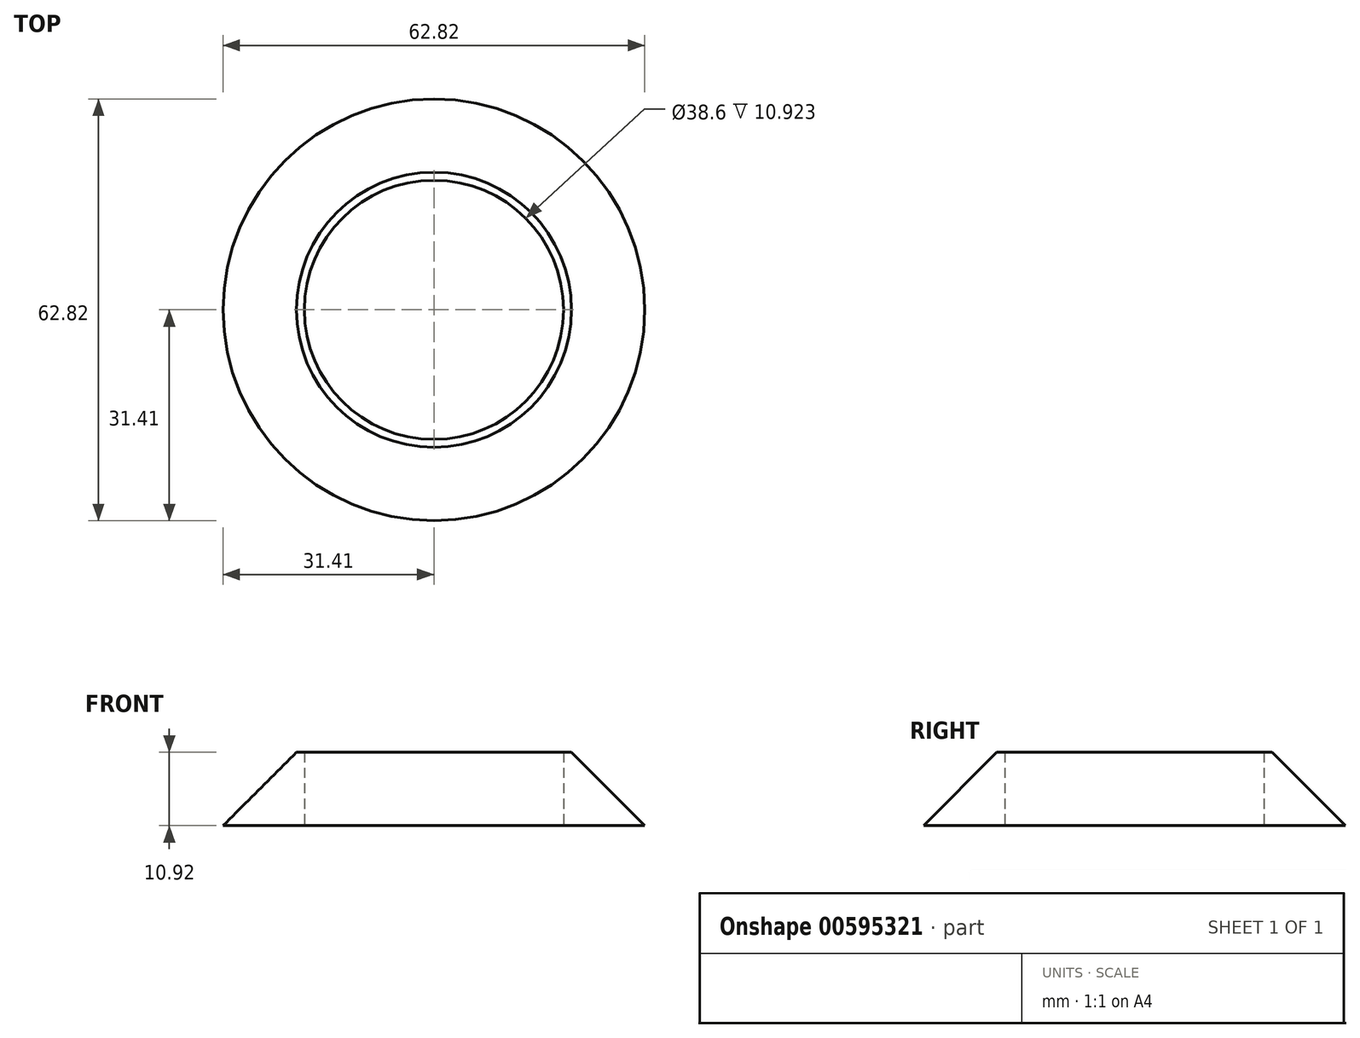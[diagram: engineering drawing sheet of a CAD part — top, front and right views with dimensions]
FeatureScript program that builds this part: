
annotation { "Feature Type Name" : "Feature", "Feature Type Description" : "" }
export const myFeature = defineFeature(function(context is Context, id is Id, definition is map)
    precondition{}
    {
        {
            var Q0;
            Q0=qCreatedBy(makeId("Front.planeOp"),FACE);
            var sketch = newSketch(context, id + "F0", { "sketchPlane" : qUnion([Q0])});
            skLineSegment(sketch, "E0", {"start": v(-19.3, 0) * mm, "end": v(-19.3, 10.92) * mm});
            skLineSegment(sketch, "E1", {"start": v(-19.3, 10.92) * mm, "end": v(-20.48, 10.92) * mm});
            skLineSegment(sketch, "E2", {"start": v(-20.48, 10.92) * mm, "end": v(-31.4, 0) * mm});
            skLineSegment(sketch, "E3", {"start": v(-31.4, 0) * mm, "end": v(-19.3, 0) * mm});
            skPoint(sketch, "E4", {"position": v(-22.25, 9.16) * mm});
            skLineSegment(sketch, "E5", {"start": v(0, 0) * mm, "end": v(0, 23.9) * mm, "construction": true});
            skSolve(sketch);
        }
        {
            var Q0;
            Q0 = qSketchRegion(id + "F0", true);
            var Q1;
            Q1=sQuery(id+"F0.wireOp",EDGE,"E5");
            revolve(context, id + "F1", {"entities" : qUnion([Q0]), "axis" : qUnion([Q1]), "revolveType" : RevolveType.FULL});
        }
    });
